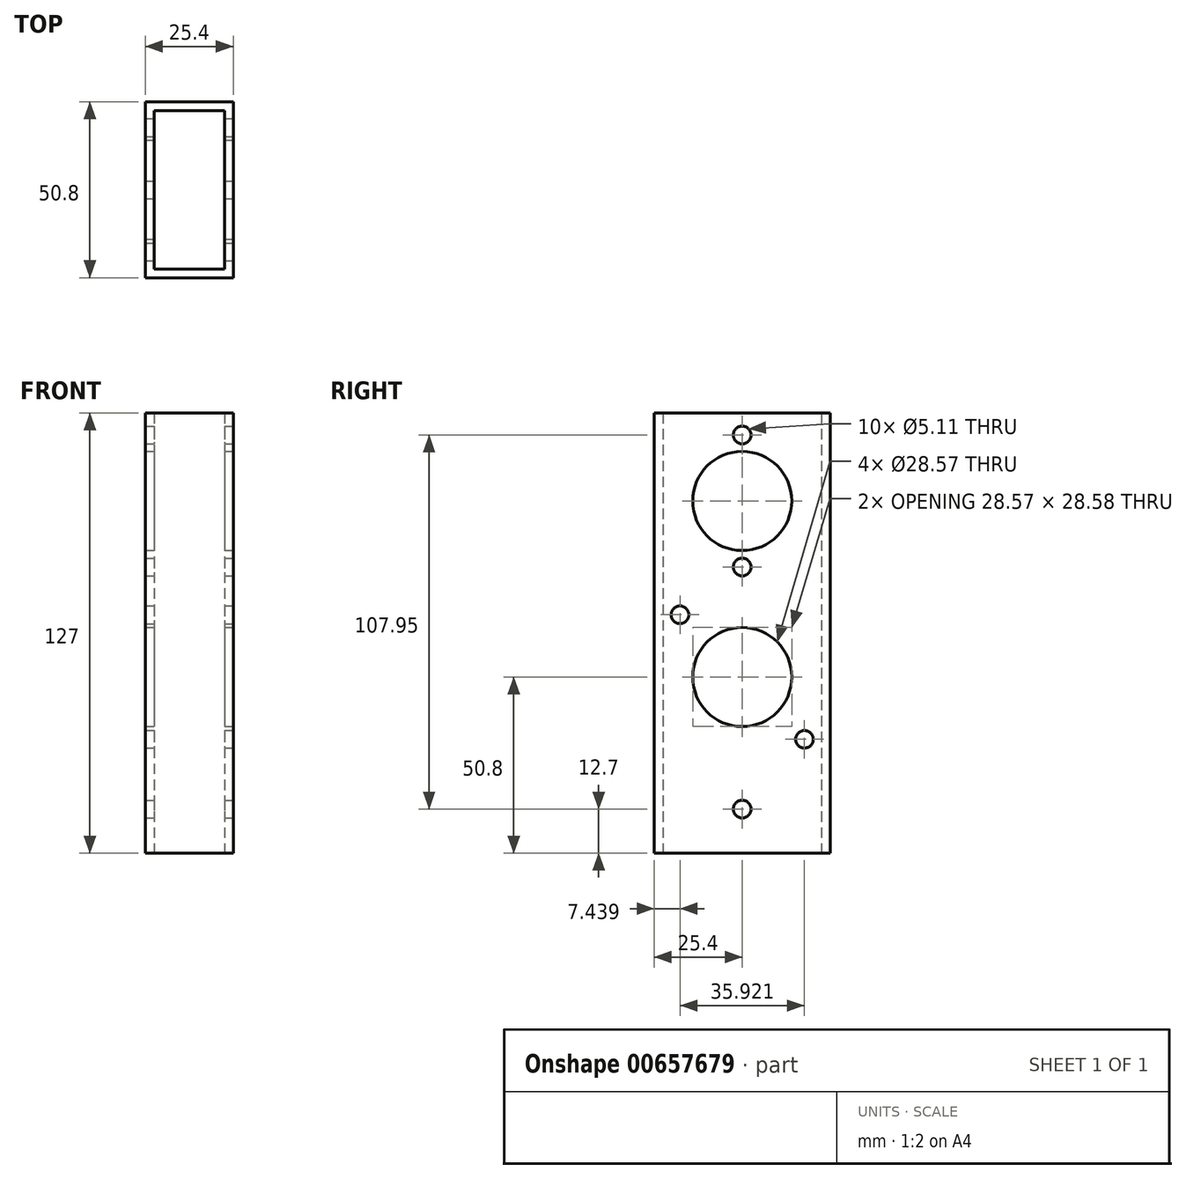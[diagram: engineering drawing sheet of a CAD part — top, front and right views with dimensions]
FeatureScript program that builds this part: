
annotation { "Feature Type Name" : "Feature", "Feature Type Description" : "" }
export const myFeature = defineFeature(function(context is Context, id is Id, definition is map)
    precondition{}
    {
        {
            var Q0;
            Q0=qCreatedBy(makeId("Top.planeOp"),FACE);
            var sketch = newSketch(context, id + "F0", { "sketchPlane" : qUnion([Q0])});
            skLineSegment(sketch, "E0.bottom", {"start": v(0, 0) * mm, "end": v(25.4, 0) * mm});
            skLineSegment(sketch, "E0.top", {"start": v(0, -50.8) * mm, "end": v(25.4, -50.8) * mm});
            skLineSegment(sketch, "E0.left", {"start": v(0, 0) * mm, "end": v(0, -50.8) * mm});
            skLineSegment(sketch, "E0.right", {"start": v(25.4, 0) * mm, "end": v(25.4, -50.8) * mm});
            skLineSegment(sketch, "E1.bottom", {"start": v(2.54, -48.26) * mm, "end": v(22.86, -48.26) * mm});
            skLineSegment(sketch, "E1.top", {"start": v(2.54, -2.54) * mm, "end": v(22.86, -2.54) * mm});
            skLineSegment(sketch, "E1.left", {"start": v(2.54, -48.26) * mm, "end": v(2.54, -2.54) * mm});
            skLineSegment(sketch, "E1.right", {"start": v(22.86, -48.26) * mm, "end": v(22.86, -2.54) * mm});
            skSolve(sketch);
        }
        {
            var Q0;
            Q0=makeQuery(id+"F0.imprint","IMPRINT",FACE,{"disambiguationData":[TD([[makeQuery(id+"F0.imprint","IMPRINT",EDGE,{"derivedFrom":sQuery(id+"F0.wireOp",EDGE,"E0.bottom")}),-1.0]])]});
            extrude(context, id + "F1", {"entities" : qUnion([Q0]), "depth" : 127 * mm, "offsetDistance" : 25.4 * mm});
        }
        {
            var Q0;
            Q0=makeQuery(id+"F1.opExtrude","SWEPT_FACE",FACE,{"disambiguationData":[OSD([sQuery(id+"F0.wireOp",EDGE,"E0.right")])]});
            var sketch = newSketch(context, id + "F2", { "sketchPlane" : qUnion([Q0])});
            skCircle(sketch, "E2", {"center": v(-25.4, 101.6) * mm, "radius": 14.29 * mm});
            skCircle(sketch, "E3", {"center": v(-25.4, 12.7) * mm, "radius": 2.55 * mm});
            skCircle(sketch, "E4.0.2.0", {"center": v(-25.4, 82.55) * mm, "radius": 2.55 * mm});
            skCircle(sketch, "E4.0.3.0", {"center": v(-25.4, 120.65) * mm, "radius": 2.55 * mm});
            skLineSegment(sketch, "E4.direction1", {"start": v(-25.4, 12.7) * mm, "end": v(0, 12.7) * mm, "construction": true});
            skCircle(sketch, "E5", {"center": v(-25.4, 50.8) * mm, "radius": 25.4 * mm});
            skCircle(sketch, "E6", {"center": v(-43.36, 68.76) * mm, "radius": 2.55 * mm});
            skCircle(sketch, "E7", {"center": v(-7.44, 32.84) * mm, "radius": 2.55 * mm});
            skLineSegment(sketch, "E8", {"start": v(-25.4, 50.8) * mm, "end": v(-43.36, 68.76) * mm});
            skLineSegment(sketch, "E9", {"start": v(-50.8, 50.8) * mm, "end": v(-25.4, 50.8) * mm});
            skLineSegment(sketch, "E10", {"start": v(-7.44, 32.84) * mm, "end": v(-25.4, 50.8) * mm});
            skCircle(sketch, "E11", {"center": v(-25.4, 50.8) * mm, "radius": 14.29 * mm});
            skSolve(sketch);
        }
        {
            var Q0;
            {var subQ0=sQuery(id+"F2.wireOp",EDGE,"E4.0.3.0");var subQ1=sQuery(id+"F2.wireOp",EDGE,"E2");var subQ2=makeQuery(id+"F2.imprint","INTERSECT",VERTEX,{"disambiguationData":[OD(0.0)],"derivedFrom":[subQ1,subQ0]});Q0=makeQuery(id+"F2.imprint","IMPRINT",FACE,{"disambiguationData":[TD([[makeQuery(id+"F2.imprint","IMPRINT",EDGE,{"disambiguationData":[TD([[subQ2,-1.0]])],"derivedFrom":subQ1}),1.0]])]});}
            var Q1;
            {var subQ0=sQuery(id+"F2.wireOp",EDGE,"E5");var subQ1=makeQuery(id+"F2.imprint","INTERSECT",VERTEX,{"derivedFrom":[subQ0,sQuery(id+"F2.wireOp",EDGE,"E8")]});Q1=makeQuery(id+"F2.imprint","IMPRINT",FACE,{"disambiguationData":[TD([[makeQuery(id+"F2.imprint","IMPRINT",EDGE,{"disambiguationData":[TD([[subQ1,1.0]])],"derivedFrom":subQ0}),-1.0]])]});}
            var Q2;
            {var subQ0=sQuery(id+"F2.wireOp",EDGE,"E4.0.3.0");var subQ1=sQuery(id+"F2.wireOp",EDGE,"E2");var subQ2=makeQuery(id+"F2.imprint","INTERSECT",VERTEX,{"disambiguationData":[OD(0.0)],"derivedFrom":[subQ1,subQ0]});Q2=makeQuery(id+"F2.imprint","IMPRINT",FACE,{"disambiguationData":[TD([[makeQuery(id+"F2.imprint","IMPRINT",EDGE,{"disambiguationData":[TD([[subQ2,1.0]])],"derivedFrom":subQ1}),1.0]])]});}
            var Q3;
            Q3=makeQuery(id+"F2.imprint","IMPRINT",FACE,{"disambiguationData":[TD([[makeQuery(id+"F2.imprint","IMPRINT",EDGE,{"derivedFrom":sQuery(id+"F2.wireOp",EDGE,"E4.0.2.0")}),1.0]])]});
            var Q4;
            Q4=makeQuery(id+"F2.imprint","IMPRINT",FACE,{"disambiguationData":[TD([[makeQuery(id+"F2.imprint","IMPRINT",EDGE,{"derivedFrom":sQuery(id+"F2.wireOp",EDGE,"E3")}),1.0]])]});
            var Q5;
            {var subQ1=sQuery(id+"F2.wireOp",EDGE,"E8");var subQ3=sQuery(id+"F2.wireOp",EDGE,"E11");var subQ4=makeQuery(id+"F2.imprint","INTERSECT",VERTEX,{"derivedFrom":[subQ1,subQ3]});Q5=makeQuery(id+"F2.imprint","IMPRINT",FACE,{"disambiguationData":[TD([[makeQuery(id+"F2.imprint","IMPRINT",EDGE,{"disambiguationData":[TD([[subQ4,1.0]])],"derivedFrom":subQ3}),1.0]])]});}
            var Q6;
            {var subQ1=sQuery(id+"F2.wireOp",EDGE,"E8");var subQ3=sQuery(id+"F2.wireOp",EDGE,"E11");var subQ4=makeQuery(id+"F2.imprint","INTERSECT",VERTEX,{"derivedFrom":[subQ1,subQ3]});Q6=makeQuery(id+"F2.imprint","IMPRINT",FACE,{"disambiguationData":[TD([[makeQuery(id+"F2.imprint","IMPRINT",EDGE,{"disambiguationData":[TD([[subQ4,-1.0]])],"derivedFrom":subQ3}),1.0]])]});}
            var Q7;
            {var subQ0=sQuery(id+"F2.wireOp",EDGE,"E8");var subQ1=sQuery(id+"F2.wireOp",EDGE,"E5");var subQ2=makeQuery(id+"F2.imprint","INTERSECT",VERTEX,{"derivedFrom":[subQ1,subQ0]});Q7=makeQuery(id+"F2.imprint","IMPRINT",FACE,{"disambiguationData":[TD([[makeQuery(id+"F2.imprint","IMPRINT",EDGE,{"disambiguationData":[TD([[subQ2,-1.0]])],"derivedFrom":subQ1}),1.0]])]});}
            var Q8;
            {var subQ0=sQuery(id+"F2.wireOp",EDGE,"E8");var subQ1=sQuery(id+"F2.wireOp",EDGE,"E5");var subQ2=makeQuery(id+"F2.imprint","INTERSECT",VERTEX,{"derivedFrom":[subQ1,subQ0]});Q8=makeQuery(id+"F2.imprint","IMPRINT",FACE,{"disambiguationData":[TD([[makeQuery(id+"F2.imprint","IMPRINT",EDGE,{"disambiguationData":[TD([[subQ2,1.0]])],"derivedFrom":subQ1}),1.0]])]});}
            var Q9;
            {var subQ1=sQuery(id+"F2.wireOp",EDGE,"E9");var subQ3=sQuery(id+"F2.wireOp",EDGE,"E11");var subQ4=makeQuery(id+"F2.imprint","INTERSECT",VERTEX,{"derivedFrom":[subQ1,subQ3]});Q9=makeQuery(id+"F2.imprint","IMPRINT",FACE,{"disambiguationData":[TD([[makeQuery(id+"F2.imprint","IMPRINT",EDGE,{"disambiguationData":[TD([[subQ4,-1.0]])],"derivedFrom":subQ3}),1.0]])]});}
            var Q10;
            {var subQ0=sQuery(id+"F2.wireOp",EDGE,"E5");var subQ1=makeQuery(id+"F2.imprint","INTERSECT",VERTEX,{"derivedFrom":[subQ0,sQuery(id+"F2.wireOp",EDGE,"E10")]});Q10=makeQuery(id+"F2.imprint","IMPRINT",FACE,{"disambiguationData":[TD([[makeQuery(id+"F2.imprint","IMPRINT",EDGE,{"disambiguationData":[TD([[subQ1,1.0]])],"derivedFrom":subQ0}),-1.0]])]});}
            var Q11;
            {var subQ0=sQuery(id+"F2.wireOp",EDGE,"E10");var subQ1=sQuery(id+"F2.wireOp",EDGE,"E5");var subQ2=makeQuery(id+"F2.imprint","INTERSECT",VERTEX,{"derivedFrom":[subQ1,subQ0]});Q11=makeQuery(id+"F2.imprint","IMPRINT",FACE,{"disambiguationData":[TD([[makeQuery(id+"F2.imprint","IMPRINT",EDGE,{"disambiguationData":[TD([[subQ2,-1.0]])],"derivedFrom":subQ1}),1.0]])]});}
            var Q12;
            {var subQ0=sQuery(id+"F2.wireOp",EDGE,"E10");var subQ1=sQuery(id+"F2.wireOp",EDGE,"E5");var subQ2=makeQuery(id+"F2.imprint","INTERSECT",VERTEX,{"derivedFrom":[subQ1,subQ0]});Q12=makeQuery(id+"F2.imprint","IMPRINT",FACE,{"disambiguationData":[TD([[makeQuery(id+"F2.imprint","IMPRINT",EDGE,{"disambiguationData":[TD([[subQ2,1.0]])],"derivedFrom":subQ1}),1.0]])]});}
            var Q13;
            Q13=makeQuery(id+"F2.imprint","IMPRINT",FACE,{"disambiguationData":[TD([[makeQuery(id+"F2.imprint","IMPRINT",EDGE,{"derivedFrom":sQuery(id+"F2.wireOp",EDGE,"E4.0.3.0")}),1.0]])]});
            var Q14;
            Q14=makeQuery(id+"F2.imprint","IMPRINT",FACE,{"disambiguationData":[TD([[makeQuery(id+"F2.imprint","IMPRINT",EDGE,{"derivedFrom":sQuery(id+"F2.wireOp",EDGE,"E2")}),1.0]])]});
            extrude(context, id + "F3", {"entities" : qUnion([Q0, Q1, Q2, Q3, Q4, Q5, Q6, Q7, Q8, Q9, Q10, Q11, Q12, Q13, Q14]), "operationType" : NewBodyOperationType.REMOVE, "oppositeDirection" : true, "depth" : 50.8 * mm, "offsetDistance" : 25.4 * mm});
        }
    });
